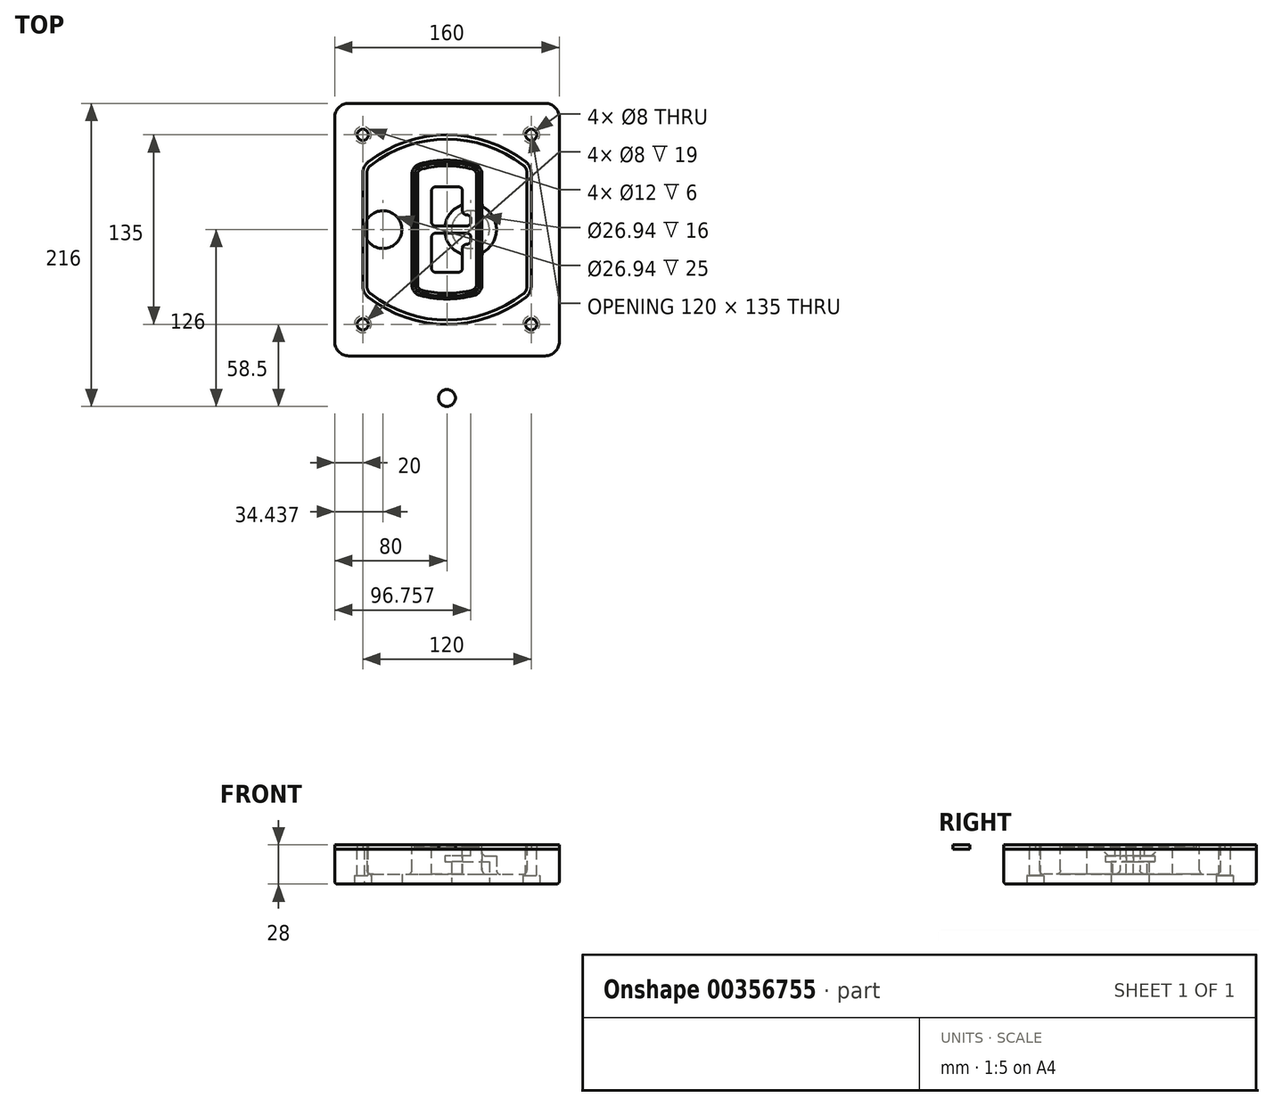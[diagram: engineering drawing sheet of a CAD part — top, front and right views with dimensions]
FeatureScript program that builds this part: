
annotation { "Feature Type Name" : "Feature", "Feature Type Description" : "" }
export const myFeature = defineFeature(function(context is Context, id is Id, definition is map)
    precondition{}
    {
        {
            var Q0;
            Q0=qCreatedBy(makeId("Top.planeOp"),FACE);
            var sketch = newSketch(context, id + "F0", { "sketchPlane" : qUnion([Q0])});
            skPoint(sketch, "E0.rect.middle", {"position": v(0, 0) * mm});
            skLineSegment(sketch, "E1.bottom", {"start": v(-70, -90) * mm, "end": v(70, -90) * mm});
            skLineSegment(sketch, "E1.top", {"start": v(-70, 90) * mm, "end": v(70, 90) * mm});
            skLineSegment(sketch, "E1.left", {"start": v(-80, -80) * mm, "end": v(-80, 80) * mm});
            skLineSegment(sketch, "E1.right", {"start": v(80, -80) * mm, "end": v(80, 80) * mm});
            skLineSegment(sketch, "E2", {"start": v(-80, 90) * mm, "end": v(80, -90) * mm, "construction": true});
            skLineSegment(sketch, "E3", {"start": v(80, 90) * mm, "end": v(-80, -90) * mm, "construction": true});
            skCircle(sketch, "E4", {"center": v(-60, 67.5) * mm, "radius": 4 * mm});
            skCircle(sketch, "E5", {"center": v(60, 67.5) * mm, "radius": 4 * mm});
            skCircle(sketch, "E6", {"center": v(60, -67.5) * mm, "radius": 4 * mm});
            skCircle(sketch, "E7", {"center": v(-60, -67.5) * mm, "radius": 4 * mm});
            skLineSegment(sketch, "E8", {"start": v(-60, 67.5) * mm, "end": v(60, 67.5) * mm, "construction": true});
            skLineSegment(sketch, "E9", {"start": v(60, 67.5) * mm, "end": v(60, -67.5) * mm, "construction": true});
            skLineSegment(sketch, "E10", {"start": v(60, -67.5) * mm, "end": v(-60, -67.5) * mm, "construction": true});
            skLineSegment(sketch, "E11", {"start": v(-60, -67.5) * mm, "end": v(-60, 67.5) * mm, "construction": true});
            skLineSegment(sketch, "E12", {"start": v(-60, 40.3) * mm, "end": v(-60, -40.3) * mm});
            skLineSegment(sketch, "E13", {"start": v(60, 40.3) * mm, "end": v(60, -40.3) * mm});
            skArc(sketch, "E14", {"start": v(56.15, 48.18) * mm, "mid": v(0, 67.5) * mm, "end": v(-56.15, 48.18) * mm});
            skArc(sketch, "E15", {"start": v(-56.15, -48.18) * mm, "mid": v(0, -67.5) * mm, "end": v(56.15, -48.18) * mm});
            skLineSegment(sketch, "E16", {"start": v(-60, 0) * mm, "end": v(60, 0) * mm, "construction": true});
            skPoint(sketch, "E17.visualSharp", {"position": v(-60, -45) * mm});
            skArc(sketch, "E17.filletArc", {"start": v(-60, -40.3) * mm, "mid": v(-58.99, -44.68) * mm, "end": v(-56.15, -48.18) * mm});
            skPoint(sketch, "E18.visualSharp", {"position": v(-60, 45) * mm});
            skArc(sketch, "E18.filletArc", {"start": v(-56.15, 48.18) * mm, "mid": v(-58.99, 44.68) * mm, "end": v(-60, 40.3) * mm});
            skPoint(sketch, "E19.visualSharp", {"position": v(60, 45) * mm});
            skArc(sketch, "E19.filletArc", {"start": v(60, 40.3) * mm, "mid": v(58.99, 44.68) * mm, "end": v(56.15, 48.18) * mm});
            skPoint(sketch, "E20.visualSharp", {"position": v(60, -45) * mm});
            skArc(sketch, "E20.filletArc", {"start": v(56.15, -48.18) * mm, "mid": v(58.99, -44.68) * mm, "end": v(60, -40.3) * mm});
            skPoint(sketch, "E21.visualSharp", {"position": v(-80, 90) * mm});
            skArc(sketch, "E21.filletArc", {"start": v(-70, 90) * mm, "mid": v(-77.07, 87.07) * mm, "end": v(-80, 80) * mm});
            skPoint(sketch, "E22.visualSharp", {"position": v(80, 90) * mm});
            skArc(sketch, "E22.filletArc", {"start": v(80, 80) * mm, "mid": v(77.07, 87.07) * mm, "end": v(70, 90) * mm});
            skPoint(sketch, "E23.visualSharp", {"position": v(80, -90) * mm});
            skArc(sketch, "E23.filletArc", {"start": v(70, -90) * mm, "mid": v(77.07, -87.07) * mm, "end": v(80, -80) * mm});
            skPoint(sketch, "E24.visualSharp", {"position": v(-80, -90) * mm});
            skArc(sketch, "E24.filletArc", {"start": v(-80, -80) * mm, "mid": v(-77.07, -87.07) * mm, "end": v(-70, -90) * mm});
            skArc(sketch, "E25.0", {"start": v(57, 40.3) * mm, "mid": v(56.3, 43.36) * mm, "end": v(54.3, 45.81) * mm});
            skLineSegment(sketch, "E25.1", {"start": v(57, 40.3) * mm, "end": v(57, -40.3) * mm});
            skArc(sketch, "E25.2", {"start": v(54.3, -45.81) * mm, "mid": v(56.3, -43.36) * mm, "end": v(57, -40.3) * mm});
            skArc(sketch, "E25.3", {"start": v(-54.3, -45.81) * mm, "mid": v(0, -64.5) * mm, "end": v(54.3, -45.81) * mm});
            skArc(sketch, "E25.4", {"start": v(-57, -40.3) * mm, "mid": v(-56.3, -43.36) * mm, "end": v(-54.3, -45.81) * mm});
            skArc(sketch, "E25.5", {"start": v(54.3, 45.81) * mm, "mid": v(0, 64.5) * mm, "end": v(-54.3, 45.81) * mm});
            skLineSegment(sketch, "E25.6", {"start": v(-57, 40.3) * mm, "end": v(-57, -40.3) * mm});
            skArc(sketch, "E25.7", {"start": v(-54.3, 45.81) * mm, "mid": v(-56.3, 43.36) * mm, "end": v(-57, 40.3) * mm});
            skArc(sketch, "E26.0", {"start": v(-58.62, 51.33) * mm, "mid": v(-62.58, 46.43) * mm, "end": v(-64, 40.3) * mm});
            skArc(sketch, "E26.1", {"start": v(58.62, 51.33) * mm, "mid": v(0, 71.5) * mm, "end": v(-58.62, 51.33) * mm});
            skArc(sketch, "E26.2", {"start": v(64, 40.3) * mm, "mid": v(62.58, 46.43) * mm, "end": v(58.62, 51.33) * mm});
            skLineSegment(sketch, "E26.3", {"start": v(64, 40.3) * mm, "end": v(64, -40.3) * mm});
            skArc(sketch, "E26.4", {"start": v(58.62, -51.33) * mm, "mid": v(62.58, -46.43) * mm, "end": v(64, -40.3) * mm});
            skLineSegment(sketch, "E26.5", {"start": v(-64, 40.3) * mm, "end": v(-64, -40.3) * mm});
            skArc(sketch, "E26.6", {"start": v(-58.62, -51.33) * mm, "mid": v(0, -71.5) * mm, "end": v(58.62, -51.33) * mm});
            skArc(sketch, "E26.7", {"start": v(-64, -40.3) * mm, "mid": v(-62.58, -46.43) * mm, "end": v(-58.62, -51.33) * mm});
            skSolve(sketch);
        }
        {
            var Q0;
            Q0=makeQuery(id+"F0.imprint","IMPRINT",FACE,{"disambiguationData":[TD([[makeQuery(id+"F0.imprint","IMPRINT",EDGE,{"derivedFrom":sQuery(id+"F0.wireOp",EDGE,"E1.bottom")}),1.0]])]});
            var Q1;
            Q1=makeQuery(id+"F0.imprint","IMPRINT",FACE,{"disambiguationData":[TD([[makeQuery(id+"F0.imprint","IMPRINT",EDGE,{"derivedFrom":sQuery(id+"F0.wireOp",EDGE,"E12")}),1.0]])]});
            var Q2;
            Q2=makeQuery(id+"F0.imprint","IMPRINT",FACE,{"disambiguationData":[TD([[makeQuery(id+"F0.imprint","IMPRINT",EDGE,{"derivedFrom":sQuery(id+"F0.wireOp",EDGE,"E25.0")}),1.0]])]});
            var Q3;
            Q3=makeQuery(id+"F0.imprint","IMPRINT",FACE,{"disambiguationData":[TD([[makeQuery(id+"F0.imprint","IMPRINT",EDGE,{"derivedFrom":sQuery(id+"F0.wireOp",EDGE,"E12")}),-1.0]])]});
            extrude(context, id + "F1", {"entities" : qUnion([Q0, Q1, Q2, Q3]), "oppositeDirection" : true, "depth" : 25 * mm});
        }
        {
            var Q0;
            Q0=makeQuery(id+"F0.imprint","IMPRINT",FACE,{"disambiguationData":[TD([[makeQuery(id+"F0.imprint","IMPRINT",EDGE,{"derivedFrom":sQuery(id+"F0.wireOp",EDGE,"E12")}),1.0]])]});
            extrude(context, id + "F2", {"entities" : qUnion([Q0]), "operationType" : NewBodyOperationType.ADD, "depth" : 3 * mm});
        }
        {
            var Q0;
            Q0=makeQuery(id+"F0.imprint","IMPRINT",FACE,{"disambiguationData":[TD([[makeQuery(id+"F0.imprint","IMPRINT",EDGE,{"derivedFrom":sQuery(id+"F0.wireOp",EDGE,"E25.0")}),1.0]])]});
            extrude(context, id + "F3", {"entities" : qUnion([Q0]), "operationType" : NewBodyOperationType.REMOVE, "oppositeDirection" : true, "depth" : 18 * mm});
        }
        {
            var Q0;
            Q0=makeQuery(id+"F2.opExtrude","CAP_FACE",FACE,{"disambiguationData":[OSD([sQuery(id+"F0.wireOp",EDGE,"E12"),sQuery(id+"F0.wireOp",EDGE,"E13"),sQuery(id+"F0.wireOp",EDGE,"E14"),sQuery(id+"F0.wireOp",EDGE,"E15"),sQuery(id+"F0.wireOp",EDGE,"E17.filletArc"),sQuery(id+"F0.wireOp",EDGE,"E18.filletArc"),sQuery(id+"F0.wireOp",EDGE,"E19.filletArc"),sQuery(id+"F0.wireOp",EDGE,"E20.filletArc"),sQuery(id+"F0.wireOp",EDGE,"E25.0"),sQuery(id+"F0.wireOp",EDGE,"E25.1"),sQuery(id+"F0.wireOp",EDGE,"E25.2"),sQuery(id+"F0.wireOp",EDGE,"E25.3"),sQuery(id+"F0.wireOp",EDGE,"E25.4"),sQuery(id+"F0.wireOp",EDGE,"E25.5"),sQuery(id+"F0.wireOp",EDGE,"E25.6"),sQuery(id+"F0.wireOp",EDGE,"E25.7")])],"isStart":false});
            var sketch = newSketch(context, id + "F4", { "sketchPlane" : qUnion([Q0])});
            skArc(sketch, "E27.0", {"start": v(-19.08, -46.97) * mm, "mid": v(0, -49.5) * mm, "end": v(19.08, -46.97) * mm});
            skArc(sketch, "E28.0", {"start": v(19.08, 46.97) * mm, "mid": v(0, 49.5) * mm, "end": v(-19.08, 46.97) * mm});
            skLineSegment(sketch, "E29", {"start": v(-25, 39.25) * mm, "end": v(-25, -39.25) * mm});
            skLineSegment(sketch, "E30", {"start": v(25, 39.25) * mm, "end": v(25, -39.25) * mm});
            skLineSegment(sketch, "E31", {"start": v(-25, 45.1) * mm, "end": v(25, 45.1) * mm, "construction": true});
            skLineSegment(sketch, "E32", {"start": v(-25, -45.1) * mm, "end": v(25, -45.1) * mm, "construction": true});
            skPoint(sketch, "E33.visualSharp", {"position": v(-25, 45.1) * mm});
            skArc(sketch, "E33.filletArc", {"start": v(-19.08, 46.97) * mm, "mid": v(-23.35, 44.11) * mm, "end": v(-25, 39.25) * mm});
            skPoint(sketch, "E34.visualSharp", {"position": v(25, 45.1) * mm});
            skArc(sketch, "E34.filletArc", {"start": v(25, 39.25) * mm, "mid": v(23.35, 44.11) * mm, "end": v(19.08, 46.97) * mm});
            skPoint(sketch, "E35.visualSharp", {"position": v(25, -45.1) * mm});
            skArc(sketch, "E35.filletArc", {"start": v(19.08, -46.97) * mm, "mid": v(23.35, -44.11) * mm, "end": v(25, -39.25) * mm});
            skPoint(sketch, "E36.visualSharp", {"position": v(-25, -45.1) * mm});
            skArc(sketch, "E36.filletArc", {"start": v(-25, -39.25) * mm, "mid": v(-23.35, -44.11) * mm, "end": v(-19.08, -46.97) * mm});
            skArc(sketch, "E37.0", {"start": v(54.3, 45.81) * mm, "mid": v(0, 64.5) * mm, "end": v(-54.3, 45.81) * mm});
            skArc(sketch, "E37.1", {"start": v(-54.3, 45.81) * mm, "mid": v(-56.3, 43.36) * mm, "end": v(-57, 40.3) * mm});
            skLineSegment(sketch, "E37.2", {"start": v(-57, 40.3) * mm, "end": v(-57, -40.3) * mm});
            skArc(sketch, "E37.3", {"start": v(-57, -40.3) * mm, "mid": v(-56.3, -43.36) * mm, "end": v(-54.3, -45.81) * mm});
            skArc(sketch, "E37.4", {"start": v(-54.3, -45.81) * mm, "mid": v(0, -64.5) * mm, "end": v(54.3, -45.81) * mm});
            skArc(sketch, "E37.5", {"start": v(54.3, -45.81) * mm, "mid": v(56.3, -43.36) * mm, "end": v(57, -40.3) * mm});
            skLineSegment(sketch, "E37.6", {"start": v(57, 40.3) * mm, "end": v(57, -40.3) * mm});
            skArc(sketch, "E37.7", {"start": v(57, 40.3) * mm, "mid": v(56.3, 43.36) * mm, "end": v(54.3, 45.81) * mm});
            skLineSegment(sketch, "E38.0", {"start": v(23, 39.25) * mm, "end": v(23, -39.25) * mm});
            skArc(sketch, "E38.1", {"start": v(18.56, -45.04) * mm, "mid": v(21.76, -42.9) * mm, "end": v(23, -39.25) * mm});
            skArc(sketch, "E38.2", {"start": v(-18.56, -45.04) * mm, "mid": v(0, -47.5) * mm, "end": v(18.56, -45.04) * mm});
            skArc(sketch, "E38.3", {"start": v(-23, -39.25) * mm, "mid": v(-21.76, -42.9) * mm, "end": v(-18.56, -45.04) * mm});
            skLineSegment(sketch, "E38.4", {"start": v(-23, 39.25) * mm, "end": v(-23, -39.25) * mm});
            skArc(sketch, "E38.5", {"start": v(23, 39.25) * mm, "mid": v(21.76, 42.9) * mm, "end": v(18.56, 45.04) * mm});
            skArc(sketch, "E38.6", {"start": v(-18.56, 45.04) * mm, "mid": v(-21.76, 42.9) * mm, "end": v(-23, 39.25) * mm});
            skArc(sketch, "E38.7", {"start": v(18.56, 45.04) * mm, "mid": v(0, 47.5) * mm, "end": v(-18.56, 45.04) * mm});
            skArc(sketch, "E39.0", {"start": v(21, 39.25) * mm, "mid": v(20.18, 41.68) * mm, "end": v(18.04, 43.1) * mm});
            skLineSegment(sketch, "E39.1", {"start": v(21, 39.25) * mm, "end": v(21, -39.25) * mm});
            skArc(sketch, "E39.2", {"start": v(18.04, -43.1) * mm, "mid": v(20.18, -41.68) * mm, "end": v(21, -39.25) * mm});
            skArc(sketch, "E39.3", {"start": v(-18.04, -43.1) * mm, "mid": v(0, -45.5) * mm, "end": v(18.04, -43.1) * mm});
            skArc(sketch, "E39.4", {"start": v(-21, -39.25) * mm, "mid": v(-20.18, -41.68) * mm, "end": v(-18.04, -43.1) * mm});
            skArc(sketch, "E39.5", {"start": v(18.04, 43.1) * mm, "mid": v(0, 45.5) * mm, "end": v(-18.04, 43.1) * mm});
            skLineSegment(sketch, "E39.6", {"start": v(-21, 39.25) * mm, "end": v(-21, -39.25) * mm});
            skArc(sketch, "E39.7", {"start": v(-18.04, 43.1) * mm, "mid": v(-20.18, 41.68) * mm, "end": v(-21, 39.25) * mm});
            skLineSegment(sketch, "E40", {"start": v(-25, 0) * mm, "end": v(25, 0) * mm, "construction": true});
            skLineSegment(sketch, "E41", {"start": v(-11, 5.5) * mm, "end": v(-11, 27.5) * mm});
            skLineSegment(sketch, "E42", {"start": v(-8, 30.5) * mm, "end": v(8, 30.5) * mm});
            skLineSegment(sketch, "E43", {"start": v(11, 27.5) * mm, "end": v(11, 13.5) * mm});
            skLineSegment(sketch, "E44", {"start": v(14, 10.5) * mm, "end": v(14, 10.5) * mm});
            skLineSegment(sketch, "E45", {"start": v(17, 7.5) * mm, "end": v(17, 5.5) * mm});
            skLineSegment(sketch, "E46", {"start": v(14, 2.5) * mm, "end": v(-8, 2.5) * mm});
            skPoint(sketch, "E47.visualSharp", {"position": v(-11, 30.5) * mm});
            skArc(sketch, "E47.filletArc", {"start": v(-8, 30.5) * mm, "mid": v(-10.12, 29.62) * mm, "end": v(-11, 27.5) * mm});
            skPoint(sketch, "E48.visualSharp", {"position": v(11, 30.5) * mm});
            skArc(sketch, "E48.filletArc", {"start": v(11, 27.5) * mm, "mid": v(10.12, 29.62) * mm, "end": v(8, 30.5) * mm});
            skPoint(sketch, "E49.visualSharp", {"position": v(11, 10.5) * mm});
            skArc(sketch, "E49.filletArc", {"start": v(11, 13.5) * mm, "mid": v(11.88, 11.38) * mm, "end": v(14, 10.5) * mm});
            skPoint(sketch, "E50.visualSharp", {"position": v(17, 10.5) * mm});
            skArc(sketch, "E50.filletArc", {"start": v(17, 7.5) * mm, "mid": v(16.12, 9.62) * mm, "end": v(14, 10.5) * mm});
            skPoint(sketch, "E51.visualSharp", {"position": v(17, 2.5) * mm});
            skArc(sketch, "E51.filletArc", {"start": v(14, 2.5) * mm, "mid": v(16.12, 3.38) * mm, "end": v(17, 5.5) * mm});
            skPoint(sketch, "E52.visualSharp", {"position": v(-11, 2.5) * mm});
            skArc(sketch, "E52.filletArc", {"start": v(-11, 5.5) * mm, "mid": v(-10.12, 3.38) * mm, "end": v(-8, 2.5) * mm});
            skLineSegment(sketch, "E53.0.MirrorCS", {"start": v(14, -2.5) * mm, "end": v(-8, -2.5) * mm});
            skArc(sketch, "E54.0.MirrorCS", {"start": v(-11, -5.5) * mm, "mid": v(-10.12, -3.38) * mm, "end": v(-8, -2.5) * mm});
            skLineSegment(sketch, "E55.0.MirrorCS", {"start": v(-11, -5.5) * mm, "end": v(-11, -27.5) * mm});
            skArc(sketch, "E56.0.MirrorCS", {"start": v(-8, -30.5) * mm, "mid": v(-10.12, -29.62) * mm, "end": v(-11, -27.5) * mm});
            skLineSegment(sketch, "E57.0.MirrorCS", {"start": v(-8, -30.5) * mm, "end": v(8, -30.5) * mm});
            skArc(sketch, "E58.0.MirrorCS", {"start": v(11, -27.5) * mm, "mid": v(10.12, -29.62) * mm, "end": v(8, -30.5) * mm});
            skLineSegment(sketch, "E59.0.MirrorCS", {"start": v(11, -27.5) * mm, "end": v(11, -13.5) * mm});
            skArc(sketch, "E60.0.MirrorCS", {"start": v(11, -13.5) * mm, "mid": v(11.88, -11.38) * mm, "end": v(14, -10.5) * mm});
            skArc(sketch, "E61.0.MirrorCS", {"start": v(17, -7.5) * mm, "mid": v(16.12, -9.62) * mm, "end": v(14, -10.5) * mm});
            skLineSegment(sketch, "E62.0.MirrorCS", {"start": v(17, -7.5) * mm, "end": v(17, -5.5) * mm});
            skArc(sketch, "E63.0.MirrorCS", {"start": v(14, -2.5) * mm, "mid": v(16.12, -3.38) * mm, "end": v(17, -5.5) * mm});
            skSolve(sketch);
        }
        {
            var Q0;
            Q0=makeQuery(id+"F4.imprint","IMPRINT",FACE,{"disambiguationData":[TD([[makeQuery(id+"F4.imprint","IMPRINT",EDGE,{"derivedFrom":sQuery(id+"F4.wireOp",EDGE,"E27.0")}),1.0]])]});
            var Q1;
            Q1=makeQuery(id+"F4.imprint","IMPRINT",FACE,{"disambiguationData":[TD([[makeQuery(id+"F4.imprint","IMPRINT",EDGE,{"derivedFrom":sQuery(id+"F4.wireOp",EDGE,"E38.0")}),-1.0]])]});
            var Q2;
            Q2=makeQuery(id+"F4.imprint","IMPRINT",FACE,{"disambiguationData":[TD([[makeQuery(id+"F4.imprint","IMPRINT",EDGE,{"derivedFrom":sQuery(id+"F4.wireOp",EDGE,"E39.0")}),1.0]])]});
            extrude(context, id + "F5", {"entities" : qUnion([Q0, Q1, Q2]), "operationType" : NewBodyOperationType.ADD, "endBound" : BoundingType.UP_TO_NEXT, "oppositeDirection" : true, "depth" : 25 * mm});
        }
        {
            var Q0;
            Q0=makeQuery(id+"F4.imprint","IMPRINT",FACE,{"disambiguationData":[TD([[makeQuery(id+"F4.imprint","IMPRINT",EDGE,{"derivedFrom":sQuery(id+"F4.wireOp",EDGE,"E38.0")}),-1.0]])]});
            extrude(context, id + "F6", {"entities" : qUnion([Q0]), "operationType" : NewBodyOperationType.REMOVE, "oppositeDirection" : true, "depth" : 2 * mm});
        }
        {
            var Q0;
            Q0=makeQuery(id+"F1.opExtrude","CAP_FACE",FACE,{"disambiguationData":[OSD([sQuery(id+"F0.wireOp",EDGE,"E1.bottom"),sQuery(id+"F0.wireOp",EDGE,"E1.top"),sQuery(id+"F0.wireOp",EDGE,"E1.left"),sQuery(id+"F0.wireOp",EDGE,"E1.right"),sQuery(id+"F0.wireOp",EDGE,"E4"),sQuery(id+"F0.wireOp",EDGE,"E5"),sQuery(id+"F0.wireOp",EDGE,"E6"),sQuery(id+"F0.wireOp",EDGE,"E7"),sQuery(id+"F0.wireOp",EDGE,"E21.filletArc"),sQuery(id+"F0.wireOp",EDGE,"E22.filletArc"),sQuery(id+"F0.wireOp",EDGE,"E23.filletArc"),sQuery(id+"F0.wireOp",EDGE,"E24.filletArc")])],"isStart":false});
            var sketch = newSketch(context, id + "F7", { "sketchPlane" : qUnion([Q0])});
            skCircle(sketch, "E64", {"center": v(16.76, 0) * mm, "radius": 13.47 * mm});
            skCircle(sketch, "E65", {"center": v(-45.56, 0) * mm, "radius": 13.47 * mm});
            skLineSegment(sketch, "E66", {"start": v(80, 0) * mm, "end": v(-80, 0) * mm});
            skCircle(sketch, "E67", {"center": v(16.76, 0) * mm, "radius": 18.47 * mm});
            skCircle(sketch, "E68", {"center": v(60, -67.5) * mm, "radius": 6 * mm});
            skCircle(sketch, "E69", {"center": v(-60, -67.5) * mm, "radius": 6 * mm});
            skCircle(sketch, "E70", {"center": v(-60, 67.5) * mm, "radius": 6 * mm});
            skCircle(sketch, "E71", {"center": v(60, 67.5) * mm, "radius": 6 * mm});
            skSolve(sketch);
        }
        {
            var Q0;
            {var subQ1=sQuery(id+"F7.wireOp",EDGE,"E66");var subQ4=sQuery(id+"F7.wireOp",EDGE,"E64");var subQ6=makeQuery(id+"F7.imprint","INTERSECT",VERTEX,{"disambiguationData":[OD(0.0)],"derivedFrom":[subQ4,subQ1]});Q0=makeQuery(id+"F7.imprint","IMPRINT",FACE,{"disambiguationData":[TD([[makeQuery(id+"F7.imprint","IMPRINT",EDGE,{"disambiguationData":[TD([[subQ6,-1.0]])],"derivedFrom":subQ4}),-1.0]])]});}
            var Q1;
            {var subQ0=sQuery(id+"F7.wireOp",EDGE,"E66");var subQ1=sQuery(id+"F7.wireOp",EDGE,"E64");var subQ3=makeQuery(id+"F7.imprint","INTERSECT",VERTEX,{"disambiguationData":[OD(0.0)],"derivedFrom":[subQ1,subQ0]});Q1=makeQuery(id+"F7.imprint","IMPRINT",FACE,{"disambiguationData":[TD([[makeQuery(id+"F7.imprint","IMPRINT",EDGE,{"disambiguationData":[TD([[subQ3,-1.0]])],"derivedFrom":subQ1}),1.0]])]});}
            var Q2;
            {var subQ0=sQuery(id+"F7.wireOp",EDGE,"E66");var subQ1=sQuery(id+"F7.wireOp",EDGE,"E64");var subQ3=makeQuery(id+"F7.imprint","INTERSECT",VERTEX,{"disambiguationData":[OD(0.0)],"derivedFrom":[subQ1,subQ0]});Q2=makeQuery(id+"F7.imprint","IMPRINT",FACE,{"disambiguationData":[TD([[makeQuery(id+"F7.imprint","IMPRINT",EDGE,{"disambiguationData":[TD([[subQ3,1.0]])],"derivedFrom":subQ1}),1.0]])]});}
            var Q3;
            {var subQ1=sQuery(id+"F7.wireOp",EDGE,"E66");var subQ4=sQuery(id+"F7.wireOp",EDGE,"E64");var subQ6=makeQuery(id+"F7.imprint","INTERSECT",VERTEX,{"disambiguationData":[OD(0.0)],"derivedFrom":[subQ4,subQ1]});Q3=makeQuery(id+"F7.imprint","IMPRINT",FACE,{"disambiguationData":[TD([[makeQuery(id+"F7.imprint","IMPRINT",EDGE,{"disambiguationData":[TD([[subQ6,1.0]])],"derivedFrom":subQ4}),-1.0]])]});}
            extrude(context, id + "F8", {"entities" : qUnion([Q0, Q1, Q2, Q3]), "operationType" : NewBodyOperationType.ADD, "oppositeDirection" : true, "depth" : 20 * mm});
        }
        {
            var Q0;
            {var subQ0=sQuery(id+"F7.wireOp",EDGE,"E66");var subQ1=sQuery(id+"F7.wireOp",EDGE,"E64");var subQ3=makeQuery(id+"F7.imprint","INTERSECT",VERTEX,{"disambiguationData":[OD(0.0)],"derivedFrom":[subQ1,subQ0]});Q0=makeQuery(id+"F7.imprint","IMPRINT",FACE,{"disambiguationData":[TD([[makeQuery(id+"F7.imprint","IMPRINT",EDGE,{"disambiguationData":[TD([[subQ3,-1.0]])],"derivedFrom":subQ1}),1.0]])]});}
            var Q1;
            {var subQ0=sQuery(id+"F7.wireOp",EDGE,"E66");var subQ1=sQuery(id+"F7.wireOp",EDGE,"E64");var subQ3=makeQuery(id+"F7.imprint","INTERSECT",VERTEX,{"disambiguationData":[OD(0.0)],"derivedFrom":[subQ1,subQ0]});Q1=makeQuery(id+"F7.imprint","IMPRINT",FACE,{"disambiguationData":[TD([[makeQuery(id+"F7.imprint","IMPRINT",EDGE,{"disambiguationData":[TD([[subQ3,1.0]])],"derivedFrom":subQ1}),1.0]])]});}
            extrude(context, id + "F9", {"entities" : qUnion([Q0, Q1]), "operationType" : NewBodyOperationType.REMOVE, "oppositeDirection" : true, "depth" : 16 * mm});
        }
        {
            var Q0;
            {var subQ0=sQuery(id+"F7.wireOp",EDGE,"E66");var subQ1=sQuery(id+"F7.wireOp",EDGE,"E65");var subQ3=makeQuery(id+"F7.imprint","INTERSECT",VERTEX,{"disambiguationData":[OD(0.0)],"derivedFrom":[subQ1,subQ0]});Q0=makeQuery(id+"F7.imprint","IMPRINT",FACE,{"disambiguationData":[TD([[makeQuery(id+"F7.imprint","IMPRINT",EDGE,{"disambiguationData":[TD([[subQ3,-1.0]])],"derivedFrom":subQ1}),1.0]])]});}
            var Q1;
            {var subQ0=sQuery(id+"F7.wireOp",EDGE,"E66");var subQ1=sQuery(id+"F7.wireOp",EDGE,"E65");var subQ3=makeQuery(id+"F7.imprint","INTERSECT",VERTEX,{"disambiguationData":[OD(0.0)],"derivedFrom":[subQ1,subQ0]});Q1=makeQuery(id+"F7.imprint","IMPRINT",FACE,{"disambiguationData":[TD([[makeQuery(id+"F7.imprint","IMPRINT",EDGE,{"disambiguationData":[TD([[subQ3,1.0]])],"derivedFrom":subQ1}),1.0]])]});}
            extrude(context, id + "F10", {"entities" : qUnion([Q0, Q1]), "operationType" : NewBodyOperationType.REMOVE, "oppositeDirection" : true, "depth" : 25 * mm});
        }
        {
            var Q0;
            Q0=makeQuery(id+"F7.imprint","IMPRINT",FACE,{"disambiguationData":[TD([[makeQuery(id+"F7.imprint","IMPRINT",EDGE,{"derivedFrom":sQuery(id+"F7.wireOp",EDGE,"E68")}),1.0]])]});
            var Q1;
            Q1=makeQuery(id+"F7.imprint","IMPRINT",FACE,{"disambiguationData":[TD([[makeQuery(id+"F7.imprint","IMPRINT",EDGE,{"derivedFrom":makeQuery(id+"F1.opExtrude","CAP_EDGE",EDGE,{"disambiguationData":[OSD([sQuery(id+"F0.wireOp",EDGE,"E5")])],"isStart":false})}),-1.0]])]});
            var Q2;
            Q2=makeQuery(id+"F7.imprint","IMPRINT",FACE,{"disambiguationData":[TD([[makeQuery(id+"F7.imprint","IMPRINT",EDGE,{"derivedFrom":sQuery(id+"F7.wireOp",EDGE,"E69")}),1.0]])]});
            var Q3;
            Q3=makeQuery(id+"F7.imprint","IMPRINT",FACE,{"disambiguationData":[TD([[makeQuery(id+"F7.imprint","IMPRINT",EDGE,{"derivedFrom":makeQuery(id+"F1.opExtrude","CAP_EDGE",EDGE,{"disambiguationData":[OSD([sQuery(id+"F0.wireOp",EDGE,"E4")])],"isStart":false})}),-1.0]])]});
            var Q4;
            Q4=makeQuery(id+"F7.imprint","IMPRINT",FACE,{"disambiguationData":[TD([[makeQuery(id+"F7.imprint","IMPRINT",EDGE,{"derivedFrom":sQuery(id+"F7.wireOp",EDGE,"E70")}),1.0]])]});
            var Q5;
            Q5=makeQuery(id+"F7.imprint","IMPRINT",FACE,{"disambiguationData":[TD([[makeQuery(id+"F7.imprint","IMPRINT",EDGE,{"derivedFrom":makeQuery(id+"F1.opExtrude","CAP_EDGE",EDGE,{"disambiguationData":[OSD([sQuery(id+"F0.wireOp",EDGE,"E7")])],"isStart":false})}),-1.0]])]});
            var Q6;
            Q6=makeQuery(id+"F7.imprint","IMPRINT",FACE,{"disambiguationData":[TD([[makeQuery(id+"F7.imprint","IMPRINT",EDGE,{"derivedFrom":sQuery(id+"F7.wireOp",EDGE,"E71")}),1.0]])]});
            var Q7;
            Q7=makeQuery(id+"F7.imprint","IMPRINT",FACE,{"disambiguationData":[TD([[makeQuery(id+"F7.imprint","IMPRINT",EDGE,{"derivedFrom":makeQuery(id+"F1.opExtrude","CAP_EDGE",EDGE,{"disambiguationData":[OSD([sQuery(id+"F0.wireOp",EDGE,"E6")])],"isStart":false})}),-1.0]])]});
            extrude(context, id + "F11", {"entities" : qUnion([Q0, Q1, Q2, Q3, Q4, Q5, Q6, Q7]), "operationType" : NewBodyOperationType.REMOVE, "oppositeDirection" : true, "depth" : 6 * mm});
        }
        {
            var Q0;
            Q0=makeQuery(id+"F9.boolean.opBoolean","COPY",FACE,{"derivedFrom":makeQuery(id+"F9.opExtrude","CAP_FACE",FACE,{"disambiguationData":[OSD([sQuery(id+"F7.wireOp",EDGE,"E64")])],"isStart":false})});
            var sketch = newSketch(context, id + "F12", { "sketchPlane" : qUnion([Q0])});
            skArc(sketch, "E72.0", {"start": v(11, 17.55) * mm, "mid": v(2.57, 11.82) * mm, "end": v(-1.54, 2.5) * mm});
            skArc(sketch, "E72.1", {"start": v(-1.54, -2.5) * mm, "mid": v(2.57, -11.82) * mm, "end": v(11, -17.55) * mm});
            skLineSegment(sketch, "E73", {"start": v(-1.54, -2.5) * mm, "end": v(14, -2.5) * mm});
            skLineSegment(sketch, "E74.0", {"start": v(14, 2.5) * mm, "end": v(-1.54, 2.5) * mm});
            skArc(sketch, "E74.1", {"start": v(14, 2.5) * mm, "mid": v(16.12, 3.38) * mm, "end": v(17, 5.5) * mm});
            skLineSegment(sketch, "E74.2", {"start": v(17, 7.5) * mm, "end": v(17, 5.5) * mm});
            skArc(sketch, "E74.3", {"start": v(17, 7.5) * mm, "mid": v(16.12, 9.62) * mm, "end": v(14, 10.5) * mm});
            skArc(sketch, "E74.4", {"start": v(11, 13.5) * mm, "mid": v(11.88, 11.38) * mm, "end": v(14, 10.5) * mm});
            skLineSegment(sketch, "E74.5", {"start": v(11, 17.55) * mm, "end": v(11, 13.5) * mm});
            skLineSegment(sketch, "E74.7", {"start": v(14, -2.5) * mm, "end": v(-1.54, -2.5) * mm});
            skArc(sketch, "E74.8", {"start": v(14, -2.5) * mm, "mid": v(16.12, -3.38) * mm, "end": v(17, -5.5) * mm});
            skLineSegment(sketch, "E74.9", {"start": v(17, -7.5) * mm, "end": v(17, -5.5) * mm});
            skArc(sketch, "E74.10", {"start": v(17, -7.5) * mm, "mid": v(16.12, -9.62) * mm, "end": v(14, -10.5) * mm});
            skArc(sketch, "E74.11", {"start": v(11, -13.5) * mm, "mid": v(11.88, -11.38) * mm, "end": v(14, -10.5) * mm});
            skLineSegment(sketch, "E74.12", {"start": v(11, -17.55) * mm, "end": v(11, -13.5) * mm});
            skPoint(sketch, "E75.orphan", {"position": v(11, -27.5) * mm});
            skPoint(sketch, "E76.orphan", {"position": v(-8, -2.5) * mm});
            skPoint(sketch, "E77.orphan", {"position": v(-8, 2.5) * mm});
            skPoint(sketch, "E78.orphan", {"position": v(11, 27.5) * mm});
            skSolve(sketch);
        }
        {
            var Q0;
            {var subQ7=sQuery(id+"F12.wireOp",EDGE,"E72.0");var subQ14=sQuery(id+"F12.wireOp",EDGE,"E72.1");var subQ16=sQuery(id+"F12.wireOp",EDGE,"E74.1");var subQ18=sQuery(id+"F12.wireOp",EDGE,"E74.8");Q0=qUnion([makeQuery(id+"F12.imprint","IMPRINT",FACE,{"disambiguationData":[TD([[makeQuery(id+"F12.imprint","IMPRINT",EDGE,{"derivedFrom":subQ7}),1.0]])]}),makeQuery(id+"F12.imprint","IMPRINT",FACE,{"disambiguationData":[TD([[makeQuery(id+"F12.imprint","IMPRINT",EDGE,{"derivedFrom":subQ14}),1.0]])]}),makeQuery(id+"F12.imprint","IMPRINT",FACE,{"disambiguationData":[TD([[makeQuery(id+"F12.imprint","IMPRINT",EDGE,{"derivedFrom":subQ16}),1.0]])]}),makeQuery(id+"F12.imprint","IMPRINT",FACE,{"disambiguationData":[TD([[makeQuery(id+"F12.imprint","IMPRINT",EDGE,{"derivedFrom":subQ18}),-1.0]])]})]);}
            var Q1;
            Q1=makeQuery(id+"F5.boolean.opBoolean","SPLIT",FACE,{"disambiguationData":[TD([makeQuery(id+"F5.opExtrude","SWEPT_FACE",FACE,{"disambiguationData":[OSD([sQuery(id+"F4.wireOp",EDGE,"E41")])]})])],"derivedFrom":makeQuery(id+"F3.boolean.opBoolean","COPY",FACE,{"derivedFrom":makeQuery(id+"F3.opExtrude","CAP_FACE",FACE,{"disambiguationData":[OSD([sQuery(id+"F0.wireOp",EDGE,"E25.0"),sQuery(id+"F0.wireOp",EDGE,"E25.1"),sQuery(id+"F0.wireOp",EDGE,"E25.2"),sQuery(id+"F0.wireOp",EDGE,"E25.3"),sQuery(id+"F0.wireOp",EDGE,"E25.4"),sQuery(id+"F0.wireOp",EDGE,"E25.5"),sQuery(id+"F0.wireOp",EDGE,"E25.6"),sQuery(id+"F0.wireOp",EDGE,"E25.7")])],"isStart":false})})});
            extrude(context, id + "F13", {"entities" : qUnion([Q0]), "operationType" : NewBodyOperationType.REMOVE, "endBound" : BoundingType.UP_TO_SURFACE, "endBoundEntityFace" : qUnion([Q1]), "depth" : 25 * mm});
        }
        {
            var Q0;
            Q0=makeQuery(id+"F3.boolean.opBoolean","COPY",EDGE,{"derivedFrom":makeQuery(id+"F3.opExtrude","CAP_EDGE",EDGE,{"disambiguationData":[OSD([sQuery(id+"F0.wireOp",EDGE,"E25.6")])],"isStart":false})});
            var Q1;
            Q1=makeQuery(id+"F8.boolean.opBoolean","INTERSECT",EDGE,{"derivedFrom":[makeQuery(id+"F5.opExtrude","SWEPT_FACE",FACE,{"disambiguationData":[OSD([sQuery(id+"F4.wireOp",EDGE,"E30")])]}),makeQuery(id+"F8.opExtrude","CAP_FACE",FACE,{"disambiguationData":[OSD([sQuery(id+"F7.wireOp",EDGE,"E67")])],"isStart":false})]});
            var Q2;
            Q2=makeQuery(id+"F8.boolean.opBoolean","INTERSECT",EDGE,{"disambiguationData":[OD(1.0)],"derivedFrom":[makeQuery(id+"F5.opExtrude","SWEPT_FACE",FACE,{"disambiguationData":[OSD([sQuery(id+"F4.wireOp",EDGE,"E30")])]}),makeQuery(id+"F8.opExtrude","SWEPT_FACE",FACE,{"disambiguationData":[OSD([sQuery(id+"F7.wireOp",EDGE,"E67")])]})]});
            var Q3;
            {var subQ0=sQuery(id+"F4.wireOp",EDGE,"E30");Q3=makeQuery(id+"F8.boolean.opBoolean","SPLIT",EDGE,{"disambiguationData":[TD([makeQuery(id+"F5.opExtrude","SWEPT_FACE",FACE,{"disambiguationData":[OSD([sQuery(id+"F4.wireOp",EDGE,"E35.filletArc")])]})])],"derivedFrom":makeQuery(id+"F5.opExtrude","CAP_EDGE",EDGE,{"disambiguationData":[OSD([subQ0])],"isStart":false})});}
            var Q4;
            {var subQ0=sQuery(id+"F0.wireOp",EDGE,"E25.7");var subQ1=sQuery(id+"F0.wireOp",EDGE,"E25.1");var subQ2=sQuery(id+"F0.wireOp",EDGE,"E25.6");var subQ3=sQuery(id+"F0.wireOp",EDGE,"E25.5");var subQ4=sQuery(id+"F0.wireOp",EDGE,"E25.4");var subQ5=sQuery(id+"F0.wireOp",EDGE,"E25.0");var subQ6=sQuery(id+"F0.wireOp",EDGE,"E25.2");var subQ7=sQuery(id+"F0.wireOp",EDGE,"E25.3");Q4=makeQuery(id+"F8.boolean.opBoolean","INTERSECT",EDGE,{"derivedFrom":[makeQuery(id+"F5.boolean.opBoolean","SPLIT",FACE,{"disambiguationData":[TD([makeQuery(id+"F2.opExtrude","SWEPT_FACE",FACE,{"disambiguationData":[OSD([subQ5])]})])],"derivedFrom":makeQuery(id+"F3.boolean.opBoolean","COPY",FACE,{"derivedFrom":makeQuery(id+"F3.opExtrude","CAP_FACE",FACE,{"disambiguationData":[OSD([subQ5,subQ1,subQ6,subQ7,subQ4,subQ3,subQ2,subQ0])],"isStart":false})})}),makeQuery(id+"F8.opExtrude","SWEPT_FACE",FACE,{"disambiguationData":[OSD([sQuery(id+"F7.wireOp",EDGE,"E67")])]})]});}
            var Q5;
            Q5=makeQuery(id+"F8.boolean.opBoolean","INTERSECT",EDGE,{"disambiguationData":[OD(0.0)],"derivedFrom":[makeQuery(id+"F5.opExtrude","SWEPT_FACE",FACE,{"disambiguationData":[OSD([sQuery(id+"F4.wireOp",EDGE,"E30")])]}),makeQuery(id+"F8.opExtrude","SWEPT_FACE",FACE,{"disambiguationData":[OSD([sQuery(id+"F7.wireOp",EDGE,"E67")])]})]});
            fillet(context, id + "F14", {"entities" : qUnion([Q0, Q1, Q2, Q3, Q4, Q5]), "radius" : 3 * mm, "tangentPropagation" : true, "allowEdgeOverflow" : false});
        }
        {
            var Q0;
            Q0=makeQuery(id+"F1.opExtrude","CAP_EDGE",EDGE,{"disambiguationData":[OSD([sQuery(id+"F0.wireOp",EDGE,"E1.bottom")])],"isStart":false});
            fillet(context, id + "F15", {"entities" : qUnion([Q0]), "radius" : 2 * mm, "tangentPropagation" : true, "allowEdgeOverflow" : false});
        }
        {
            var Q0;
            {var subQ0=sQuery(id+"F0.wireOp",EDGE,"E21.filletArc");var subQ1=sQuery(id+"F0.wireOp",EDGE,"E7");var subQ2=sQuery(id+"F0.wireOp",EDGE,"E6");var subQ3=sQuery(id+"F0.wireOp",EDGE,"E5");var subQ4=sQuery(id+"F0.wireOp",EDGE,"E4");var subQ5=sQuery(id+"F0.wireOp",EDGE,"E22.filletArc");var subQ6=sQuery(id+"F0.wireOp",EDGE,"E1.bottom");var subQ7=sQuery(id+"F0.wireOp",EDGE,"E1.right");var subQ8=sQuery(id+"F0.wireOp",EDGE,"E1.top");var subQ9=sQuery(id+"F0.wireOp",EDGE,"E1.left");var subQ10=sQuery(id+"F0.wireOp",EDGE,"E23.filletArc");var subQ11=sQuery(id+"F0.wireOp",EDGE,"E24.filletArc");Q0=makeQuery(id+"F2.boolean.opBoolean","SPLIT",FACE,{"disambiguationData":[TD([makeQuery(id+"F1.opExtrude","SWEPT_FACE",FACE,{"disambiguationData":[OSD([subQ6])]})])],"derivedFrom":makeQuery(id+"F1.opExtrude","CAP_FACE",FACE,{"disambiguationData":[OSD([subQ6,subQ8,subQ9,subQ7,subQ4,subQ3,subQ2,subQ1,subQ0,subQ5,subQ10,subQ11])],"isStart":true})});}
            var sketch = newSketch(context, id + "F16", { "sketchPlane" : qUnion([Q0])});
            skLineSegment(sketch, "E79", {"start": v(-33, 90) * mm, "end": v(-15, 108) * mm});
            skLineSegment(sketch, "E80", {"start": v(-15, 108) * mm, "end": v(-15, 120) * mm});
            skArc(sketch, "E81", {"start": v(15, 120) * mm, "mid": v(0, 135) * mm, "end": v(-15, 120) * mm});
            skLineSegment(sketch, "E82", {"start": v(15, 120) * mm, "end": v(15, 108) * mm});
            skLineSegment(sketch, "E83", {"start": v(15, 108) * mm, "end": v(33, 90) * mm});
            skCircle(sketch, "E84", {"center": v(0, 120) * mm, "radius": 6 * mm});
            skLineSegment(sketch, "E85", {"start": v(0, 120) * mm, "end": v(0, 90) * mm, "construction": true});
            skLineSegment(sketch, "E86", {"start": v(-80, 0) * mm, "end": v(80, 0) * mm, "construction": true});
            skArc(sketch, "E87.MirrorCS", {"start": v(-15, 120) * mm, "mid": v(0, 135) * mm, "end": v(15, 120) * mm});
            skLineSegment(sketch, "E88.MirrorCS", {"start": v(15, 108) * mm, "end": v(15, 120) * mm});
            skLineSegment(sketch, "E89.MirrorCS", {"start": v(-15, 108) * mm, "end": v(-33, 90) * mm});
            skLineSegment(sketch, "E90.MirrorCS", {"start": v(33, 90) * mm, "end": v(15, 108) * mm});
            skLineSegment(sketch, "E91.MirrorCS", {"start": v(-15, 120) * mm, "end": v(-15, 108) * mm});
            skLineSegment(sketch, "E92.MirrorCS", {"start": v(-33, -90) * mm, "end": v(-15, -108) * mm});
            skLineSegment(sketch, "E93.MirrorCS", {"start": v(15, -120) * mm, "end": v(15, -108) * mm});
            skLineSegment(sketch, "E94.MirrorCS", {"start": v(-15, -108) * mm, "end": v(-15, -120) * mm});
            skLineSegment(sketch, "E95.MirrorCS", {"start": v(15, -108) * mm, "end": v(33, -90) * mm});
            skCircle(sketch, "E96.MirrorC", {"center": v(0, -120) * mm, "radius": 6 * mm});
            skArc(sketch, "E97.MirrorCS", {"start": v(15, -120) * mm, "mid": v(0, -135) * mm, "end": v(-15, -120) * mm});
            skLineSegment(sketch, "E98.MirrorCS", {"start": v(-15, -108) * mm, "end": v(-33, -90) * mm});
            skLineSegment(sketch, "E99.MirrorCS", {"start": v(33, -90) * mm, "end": v(15, -108) * mm});
            skLineSegment(sketch, "E100.MirrorCS", {"start": v(-15, -120) * mm, "end": v(-15, -108) * mm});
            skLineSegment(sketch, "E101.MirrorCS", {"start": v(0, -120) * mm, "end": v(0, -90) * mm, "construction": true});
            skLineSegment(sketch, "E102.MirrorCS", {"start": v(15, -108) * mm, "end": v(15, -120) * mm});
            skArc(sketch, "E103.MirrorCS", {"start": v(-15, -120) * mm, "mid": v(0, -135) * mm, "end": v(15, -120) * mm});
            skSolve(sketch);
        }
        {
            var Q0;
            Q0=makeQuery(id+"F16.imprint","IMPRINT",FACE,{"disambiguationData":[TD([[makeQuery(id+"F16.imprint","IMPRINT",EDGE,{"derivedFrom":sQuery(id+"F16.wireOp",EDGE,"E96.MirrorC")}),1.0]])]});
            var Q1;
            Q1=makeQuery(id+"F16.imprint","IMPRINT",FACE,{"disambiguationData":[TD([[makeQuery(id+"F16.imprint","IMPRINT",EDGE,{"derivedFrom":makeQuery(id+"F1.opExtrude","CAP_EDGE",EDGE,{"disambiguationData":[OSD([sQuery(id+"F0.wireOp",EDGE,"E1.left")])],"isStart":true})}),-1.0]])]});
            var Q2;
            Q2=makeQuery(id+"F16.imprint","IMPRINT",FACE,{"disambiguationData":[TD([[makeQuery(id+"F16.imprint","IMPRINT",EDGE,{"derivedFrom":sQuery(id+"F16.wireOp",EDGE,"E87.MirrorCS")}),-1.0]])]});
            var Q3;
            {var subQ0=sQuery(id+"F4.wireOp",EDGE,"E36.filletArc");var subQ1=sQuery(id+"F4.wireOp",EDGE,"E35.filletArc");var subQ2=sQuery(id+"F4.wireOp",EDGE,"E34.filletArc");var subQ3=sQuery(id+"F4.wireOp",EDGE,"E33.filletArc");var subQ4=sQuery(id+"F4.wireOp",EDGE,"E27.0");var subQ5=sQuery(id+"F4.wireOp",EDGE,"E30");var subQ6=sQuery(id+"F4.wireOp",EDGE,"E28.0");var subQ7=sQuery(id+"F4.wireOp",EDGE,"E29");Q3=makeQuery(id+"F6.boolean.opBoolean","SPLIT",FACE,{"disambiguationData":[TD([makeQuery(id+"F5.opExtrude","SWEPT_FACE",FACE,{"disambiguationData":[OSD([subQ4])]})])],"derivedFrom":makeQuery(id+"F5.opExtrude","CAP_FACE",FACE,{"disambiguationData":[OSD([subQ4,subQ6,subQ7,subQ5,subQ3,subQ2,subQ1,subQ0,sQuery(id+"F4.wireOp",EDGE,"E41"),sQuery(id+"F4.wireOp",EDGE,"E42"),sQuery(id+"F4.wireOp",EDGE,"E43"),sQuery(id+"F4.wireOp",EDGE,"E45"),sQuery(id+"F4.wireOp",EDGE,"E46"),sQuery(id+"F4.wireOp",EDGE,"E47.filletArc"),sQuery(id+"F4.wireOp",EDGE,"E48.filletArc"),sQuery(id+"F4.wireOp",EDGE,"E49.filletArc"),sQuery(id+"F4.wireOp",EDGE,"E50.filletArc"),sQuery(id+"F4.wireOp",EDGE,"E51.filletArc"),sQuery(id+"F4.wireOp",EDGE,"E52.filletArc"),sQuery(id+"F4.wireOp",EDGE,"E53.0.MirrorCS"),sQuery(id+"F4.wireOp",EDGE,"E54.0.MirrorCS"),sQuery(id+"F4.wireOp",EDGE,"E55.0.MirrorCS"),sQuery(id+"F4.wireOp",EDGE,"E56.0.MirrorCS"),sQuery(id+"F4.wireOp",EDGE,"E57.0.MirrorCS"),sQuery(id+"F4.wireOp",EDGE,"E58.0.MirrorCS"),sQuery(id+"F4.wireOp",EDGE,"E59.0.MirrorCS"),sQuery(id+"F4.wireOp",EDGE,"E60.0.MirrorCS"),sQuery(id+"F4.wireOp",EDGE,"E61.0.MirrorCS"),sQuery(id+"F4.wireOp",EDGE,"E62.0.MirrorCS"),sQuery(id+"F4.wireOp",EDGE,"E63.0.MirrorCS")])],"isStart":true})});}
            extrude(context, id + "F17", {"entities" : qUnion([Q0, Q1, Q2]), "endBound" : BoundingType.UP_TO_SURFACE, "endBoundEntityFace" : qUnion([Q3]), "depth" : 25 * mm});
        }
    });
